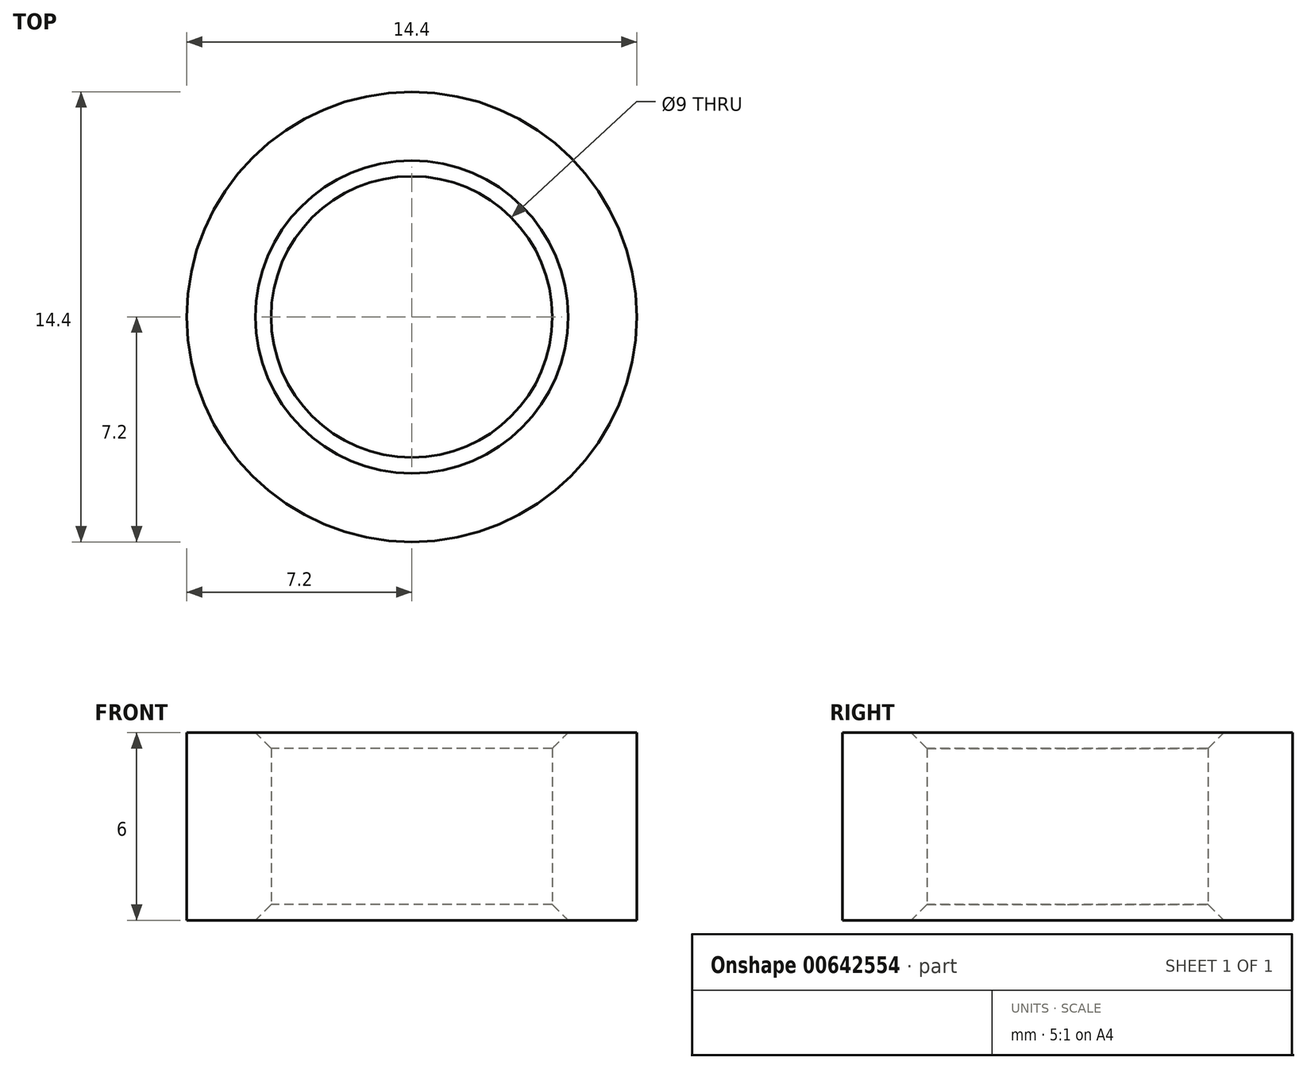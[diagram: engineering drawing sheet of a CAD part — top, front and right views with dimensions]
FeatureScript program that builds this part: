
annotation { "Feature Type Name" : "Feature", "Feature Type Description" : "" }
export const myFeature = defineFeature(function(context is Context, id is Id, definition is map)
    precondition{}
    {
        {
            var Q0;
            Q0=qCreatedBy(makeId("Top.planeOp"),FACE);
            var sketch = newSketch(context, id + "F0", { "sketchPlane" : qUnion([Q0])});
            skCircle(sketch, "E0", {"center": v(0, 0) * mm, "radius": 7.2 * mm});
            skCircle(sketch, "E1", {"center": v(0, 0) * mm, "radius": 4.5 * mm});
            skSolve(sketch);
        }
        {
            var Q0;
            Q0=makeQuery(id+"F0.imprint","IMPRINT",FACE,{"disambiguationData":[TD([[makeQuery(id+"F0.imprint","IMPRINT",EDGE,{"derivedFrom":sQuery(id+"F0.wireOp",EDGE,"E0")}),1.0]])]});
            extrude(context, id + "F1", {"entities" : qUnion([Q0]), "depth" : 6 * mm, "offsetDistance" : 25.4 * mm});
        }
        {
            var Q0;
            Q0=makeQuery(id+"F1.opExtrude","CAP_EDGE",EDGE,{"disambiguationData":[OSD([sQuery(id+"F0.wireOp",EDGE,"E1")])],"isStart":true});
            var Q1;
            Q1=makeQuery(id+"F1.opExtrude","SWEPT_FACE",FACE,{"disambiguationData":[OSD([sQuery(id+"F0.wireOp",EDGE,"E1")])]});
            chamfer(context, id + "F2", {"entities" : qUnion([Q0, Q1]), "chamferType" : ChamferType.OFFSET_ANGLE, "width" : 0.5 * mm, "oppositeDirection" : false, "angle" : 45 * degree, "tangentPropagation" : true});
        }
    });
